# Revit family: O14752711_Lavamanos Granito Vessel
name_source: partatom
category: Plumbing Fixtures
units: mm (PartAtom-declared; Revit-internal decimal feet)

## family parameters
Cut with Voids When Loaded = No
Host = Face
OmniClass Number = 23.31.13.11
OmniClass Title = Single Sinks
Part Type = Normal
Room Calculation Point = No
Round Connector Dimension = Use Diameter
Shared = No

## types (1)
- O14752711_Lavamanos Granito Vessel
    Alto = 140 mm  [stored 0.459318 ft]
    Ancho = 375 mm  [stored 1.23031 ft]
    Creado por = BIMBAU
    Default Elevation = 1219 mm
    Description = Un lavamanos ideal para espacios naturales porque la similitud al granito harán de sus espacios diseños vanguardistas e innovadores
    Dimensiones del Pozo = 3 3/4” x 4 3/4” (35.5 cm x 12 cm)
    Dimensiones del Producto Empacado = 16 1/8” x 16 1/8” x 6 1/4” (41 cm x 41 cm x 16 cm)
    Fecha de creación = 12/03/2021
    Garantía = Garantía Integral de por vida.
    Manufacturer = Corona
    Material = Corona_Porcelana_Sanitaria_Arena
    Material 2 = Corona_Plastico_Cromado
    Model = Lavamanos tipo Vessel en Porcelana Sanitaria
    Peso del Producto Empacado = 5,5 Kg
    Profundidad = 375 mm  [stored 1.23031 ft]
    Referencia = 014752711
    URL = https://corona.co

note: [stored X ft] marks values corroborated as IEEE doubles in the binary element streams (Revit-internal decimal feet)

## geometry (parser evidence)
native form markers: Sweep x8
no freeform markers — native parametric forms only
